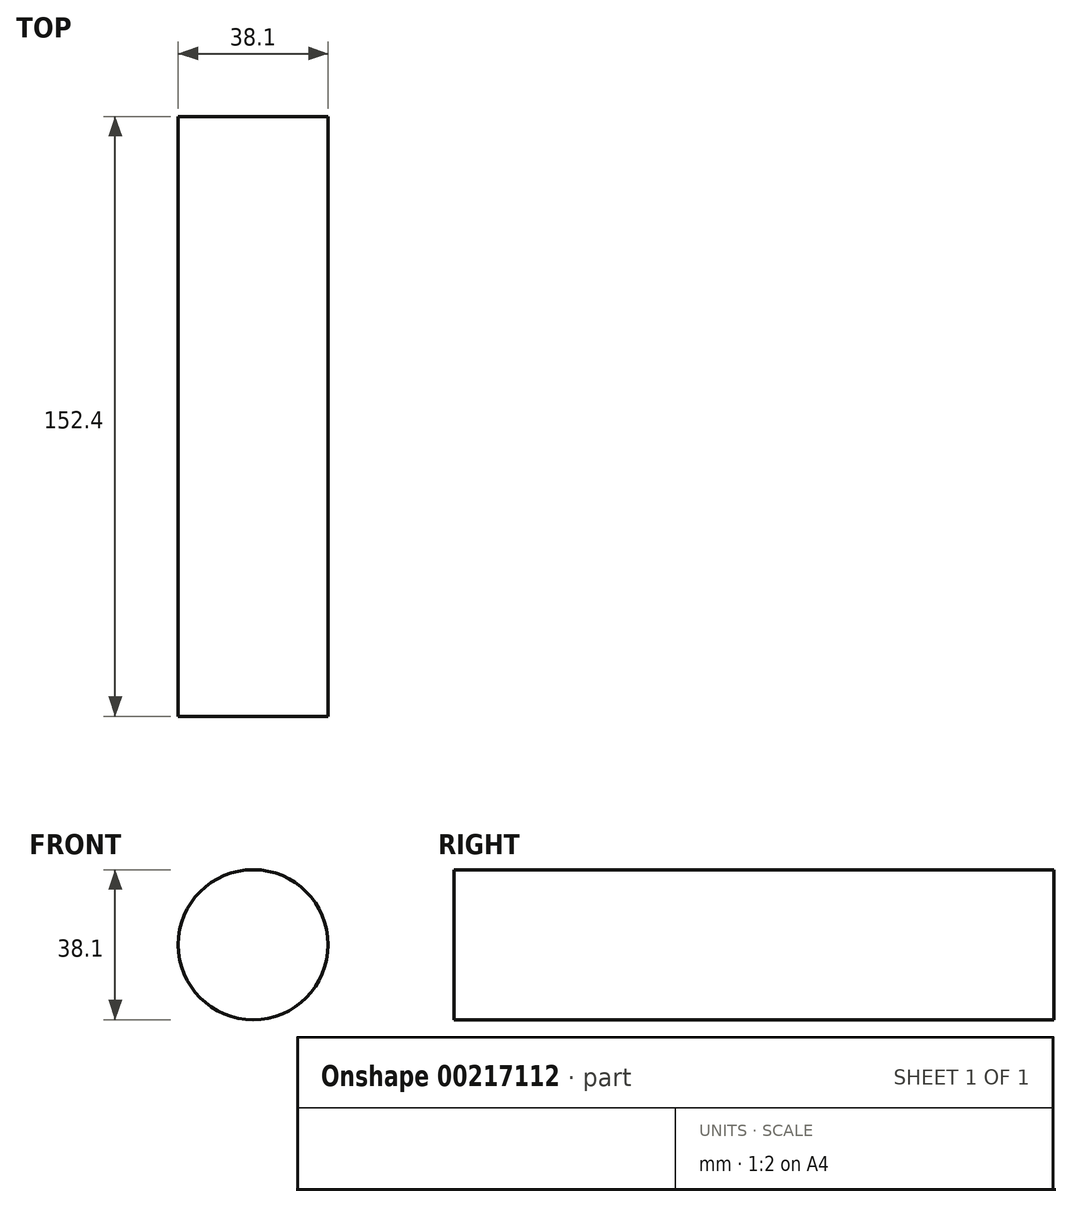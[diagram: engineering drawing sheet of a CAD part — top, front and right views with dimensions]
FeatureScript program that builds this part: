
annotation { "Feature Type Name" : "Feature", "Feature Type Description" : "" }
export const myFeature = defineFeature(function(context is Context, id is Id, definition is map)
    precondition{}
    {
        {
            var Q0;
            Q0=qCreatedBy(makeId("Front.planeOp"),FACE);
            var sketch = newSketch(context, id + "F0", { "sketchPlane" : qUnion([Q0])});
            skCircle(sketch, "E0", {"center": v(0, 0) * mm, "radius": 19.05 * mm});
            skSolve(sketch);
        }
        {
            var Q0;
            Q0 = qSketchRegion(id + "F0", true);
            extrude(context, id + "F1", {"entities" : qUnion([Q0]), "depth" : 152.4 * mm});
        }
    });
